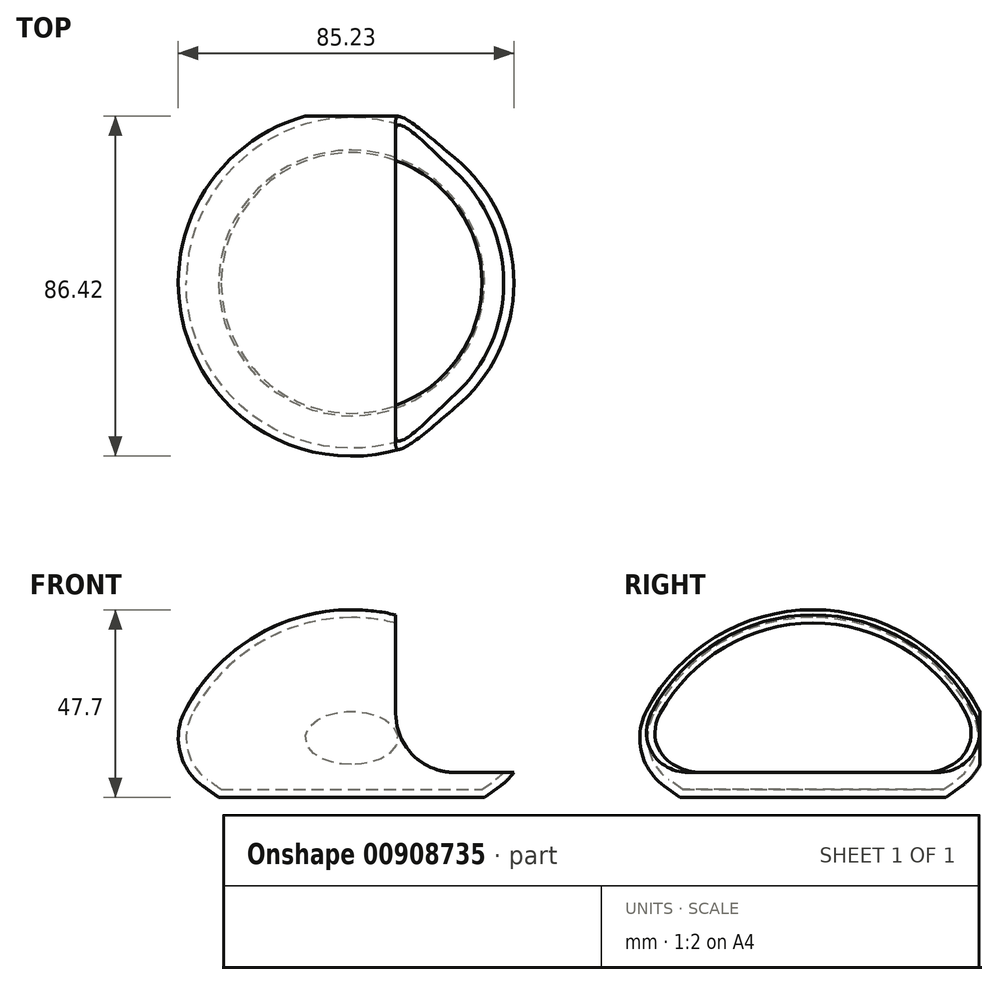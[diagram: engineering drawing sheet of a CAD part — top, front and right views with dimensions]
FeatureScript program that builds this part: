
annotation { "Feature Type Name" : "Feature", "Feature Type Description" : "" }
export const myFeature = defineFeature(function(context is Context, id is Id, definition is map)
    precondition{}
    {
        {
            var Q0;
            Q0=qCreatedBy(makeId("Front.planeOp"),FACE);
            var sketch = newSketch(context, id + "F0", { "sketchPlane" : qUnion([Q0])});
            skLineSegment(sketch, "E0", {"start": v(0, 0) * mm, "end": v(-33.75, 0) * mm});
            skLineSegment(sketch, "E1", {"start": v(0, 0) * mm, "end": v(0, 47.7) * mm, "construction": true});
            skArc(sketch, "E2", {"start": v(0, 47.7) * mm, "mid": v(-24.76, 40.77) * mm, "end": v(-42.32, 22) * mm});
            skLineSegment(sketch, "E3", {"start": v(0, 47.7) * mm, "end": v(-77.7, 47.7) * mm, "construction": true});
            skLineSegment(sketch, "E4", {"start": v(-33.75, 0) * mm, "end": v(-37.8, 2.93) * mm});
            skPoint(sketch, "E5.visualSharp", {"position": v(-46.76, 9.4) * mm});
            skArc(sketch, "E5.filletArc", {"start": v(-42.32, 22) * mm, "mid": v(-43.6, 11.63) * mm, "end": v(-37.8, 2.93) * mm});
            skArc(sketch, "E6.0", {"start": v(0, 45.7) * mm, "mid": v(-23.72, 39.06) * mm, "end": v(-40.55, 21.08) * mm});
            skArc(sketch, "E6.1", {"start": v(-40.55, 21.08) * mm, "mid": v(-41.66, 12.09) * mm, "end": v(-36.63, 4.55) * mm});
            skLineSegment(sketch, "E6.2", {"start": v(-33.1, 2) * mm, "end": v(-36.63, 4.55) * mm});
            skLineSegment(sketch, "E6.3", {"start": v(0, 2) * mm, "end": v(-33.1, 2) * mm});
            skLineSegment(sketch, "E7", {"start": v(0, 45.7) * mm, "end": v(0, 47.7) * mm});
            skLineSegment(sketch, "E8", {"start": v(0, 2) * mm, "end": v(0, 0) * mm});
            skSolve(sketch);
        }
        {
            var Q0;
            Q0 = qSketchRegion(id + "F0", true);
            var Q1;
            Q1=sQuery(id+"F0.wireOp",EDGE,"E1");
            revolve(context, id + "F1", {"surfaceOperationType" : NewSurfaceOperationType.NEW, "entities" : qUnion([Q0]), "axis" : qUnion([Q1]), "revolveType" : RevolveType.FULL});
        }
        {
            var Q0;
            Q0=qCreatedBy(makeId("Front.planeOp"),FACE);
            var sketch = newSketch(context, id + "F2", { "sketchPlane" : qUnion([Q0])});
            skArc(sketch, "E9", {"start": v(42.32, 22) * mm, "mid": v(29.4, 37.56) * mm, "end": v(11.22, 46.36) * mm});
            skArc(sketch, "E10", {"start": v(41.22, 6.36) * mm, "mid": v(43.98, 14.03) * mm, "end": v(42.32, 22) * mm});
            skLineSegment(sketch, "E11", {"start": v(11.22, 46.36) * mm, "end": v(11.22, 21.36) * mm});
            skLineSegment(sketch, "E12", {"start": v(26.22, 6.36) * mm, "end": v(41.22, 6.36) * mm});
            skPoint(sketch, "E13.visualSharp", {"position": v(11.22, 6.36) * mm});
            skArc(sketch, "E13.filletArc", {"start": v(11.22, 21.36) * mm, "mid": v(15.6, 10.76) * mm, "end": v(26.22, 6.36) * mm});
            skSolve(sketch);
        }
        {
            var Q0;
            Q0 = qSketchRegion(id + "F2", true);
            extrude(context, id + "F3", {"entities" : qUnion([Q0]), "operationType" : NewBodyOperationType.REMOVE, "endBound" : BoundingType.THROUGH_ALL, "oppositeDirection" : true, "depth" : 25 * mm, "offsetDistance" : 25 * mm, "hasSecondDirection" : true, "secondDirectionBound" : SecondDirectionBoundingType.THROUGH_ALL, "secondDirectionOppositeDirection" : false, "secondDirectionDepth" : 25 * mm});
        }
        {
            var Q0;
            Q0=qCreatedBy(makeId("Right.planeOp"),FACE);
            var sketch = newSketch(context, id + "F4", { "sketchPlane" : qUnion([Q0])});
            skArc(sketch, "E14", {"start": v(37.8, 2.93) * mm, "mid": v(43.6, 11.63) * mm, "end": v(42.32, 22) * mm});
            skArc(sketch, "E15", {"start": v(42.32, 22) * mm, "mid": v(0, 47.7) * mm, "end": v(-42.32, 22) * mm});
            skLineSegment(sketch, "E16", {"start": v(42.4, 8.34) * mm, "end": v(42.4, 21.84) * mm});
            skSolve(sketch);
        }
        {
            var Q0;
            Q0 = qSketchRegion(id + "F4", true);
            extrude(context, id + "F5", {"entities" : qUnion([Q0]), "operationType" : NewBodyOperationType.REMOVE, "oppositeDirection" : true, "depth" : 25 * mm, "offsetDistance" : 25 * mm, "hasSecondDirection" : true, "secondDirectionOppositeDirection" : false, "secondDirectionDepth" : 25 * mm});
        }
    });
